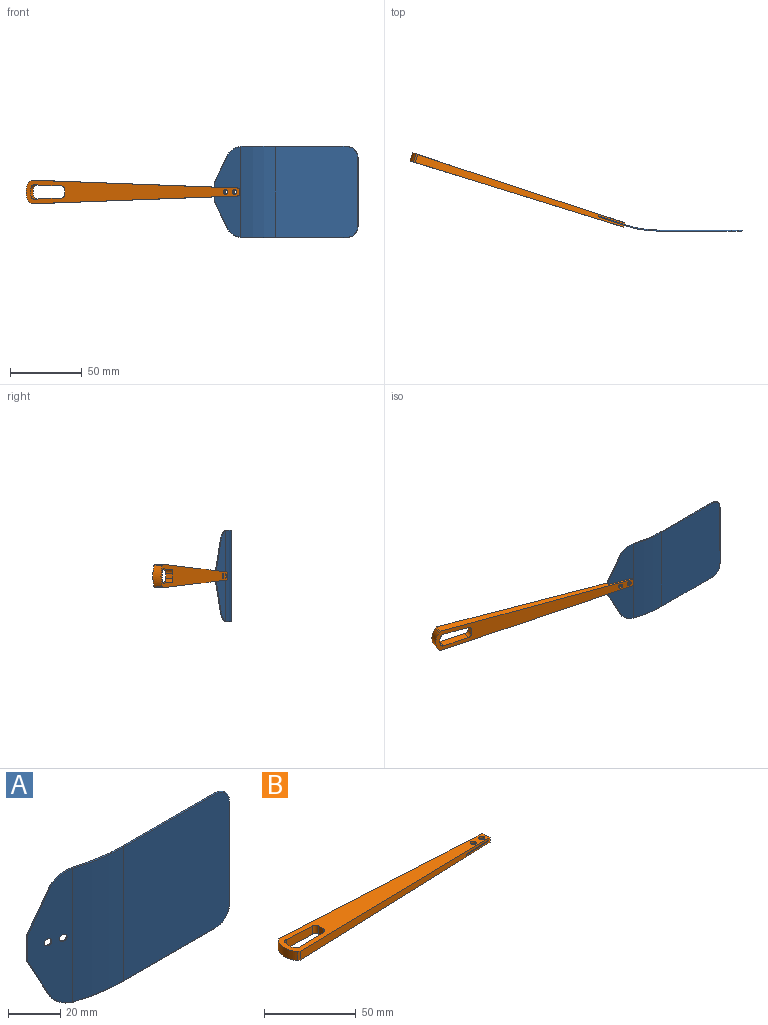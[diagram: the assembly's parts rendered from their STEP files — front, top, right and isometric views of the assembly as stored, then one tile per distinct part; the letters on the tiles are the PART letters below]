
ASSEMBLY  parts=2 mates=1
PART A: 24 faces, bbox 100.9x11.4x65.5 mm
  f0: plane 62.81x18.59mm, normal (-0.31,-0.95,0), area 862.8mm2, adj f1,f6,f7,f8,f9,f10,f21,f23
  f1: cylinder r=76.2mm len=62.89mm, axis (0,0,-1), area 1525.4mm2, adj f0,f2,f12,f13,f19,f22
  f2: plane 62.89x57.31mm, normal (0,-1,0), area 3581.6mm2, adj f1,f14,f15,f16,f17,f18
  f3: plane 62.89x57.31mm, normal (0,1,0), area 3581.6mm2, adj f4,f14,f15,f16,f17,f18
  f4: cylinder r=75.59mm len=62.89mm, axis (0,0,-1), area 1513.2mm2, adj f3,f5,f11,f12,f19,f20
  f5: plane 62.81x18.59mm, normal (0.31,0.95,0), area 862.8mm2, adj f4,f6,f7,f8,f9,f10,f21,f23
  f6: plane 12.7x0.58mm, normal (-0.95,0.31,0), area 7.6mm2, adj f0,f5,f9,f23
  f7: cylinder r=1.61mm len=3.25mm, axis (0.31,0.95,0), area 6.2mm2, adj f0,f5
  f8: cylinder r=1.61mm len=3.25mm, axis (0.31,0.95,0), area 6.2mm2, adj f0,f5
  f9: cylinder r=0.3mm len=19.06mm, axis (-0.42,0.14,0.89), area 19.9mm2, adj f0,f5,f6,f10
  f10: torus R=12.4mm, axis (0.31,0.95,0), area 12.4mm2, adj f0,f5,f9,f11,f13
  f11: bspline ~4.86x1.83mm, area 0.5mm2, adj f4,f10,f12,f13
  f12: torus R=75.9mm, axis (0,0,1), area 22.2mm2, adj f1,f4,f11,f13,f14
  f13: bspline ~4.87x1.83mm, area 0.5mm2, adj f1,f10,f11,f12
  f14: cylinder r=0.3mm len=50mm, axis (-1,0,0), area 47.9mm2, adj f2,f3,f12,f15
  f15: torus R=7.32mm, axis (0,1,0), area 11.3mm2, adj f2,f3,f14,f16
  f16: cylinder r=0.3mm len=48.26mm, axis (0,0,-1), area 46.2mm2, adj f2,f3,f15,f17
  f17: torus R=7.32mm, axis (0,1,0), area 11.3mm2, adj f2,f3,f16,f18
  f18: cylinder r=0.3mm len=50mm, axis (1,0,0), area 47.9mm2, adj f2,f3,f17,f19
  f19: torus R=75.9mm, axis (0,0,1), area 22.2mm2, adj f1,f4,f18,f20,f22
  f20: bspline ~4.86x1.83mm, area 0.5mm2, adj f4,f19,f21,f22
  f21: torus R=12.4mm, axis (0.31,0.95,0), area 12.4mm2, adj f0,f5,f20,f22,f23
  f22: bspline ~4.87x1.83mm, area 0.5mm2, adj f1,f19,f20,f21
  f23: cylinder r=0.3mm len=19.06mm, axis (-0.42,0.14,-0.89), area 19.9mm2, adj f0,f5,f6,f21
PART B: 24 faces, bbox 155.5x16.5x6 mm
  f0: plane 5.43x1.28mm, normal (1,0,0), area 7mm2, adj f1,f2,f13,f21
  f1: plane 151.61x5.88mm, normal (0.04,1,0), area 675.4mm2, adj f0,f11,f13,f14,f20,f21,f22,f23
  f2: plane 151.61x5.88mm, normal (0.04,-1,0), area 675.4mm2, adj f0,f11,f13,f14,f19,f21,f22,f23
  f3: cylinder r=1.61mm len=3.23mm, axis (0,0,-1), area 13mm2, adj f13,f21
  f4: cylinder r=1.61mm len=3.23mm, axis (0,0,-1), area 14.8mm2, adj f14,f22
  f5: cylinder r=1.61mm len=3.23mm, axis (0,0,-1), area 13mm2, adj f13,f21
  f6: cylinder r=1.61mm len=3.23mm, axis (0,0,-1), area 13.6mm2, adj f14,f22
  f7: cylinder r=12.73mm len=15.18mm, axis (0,0,-1), area 96.6mm2, adj f13,f14,f19,f20
  f8: cylinder r=9.57mm len=6.6mm, axis (0,0,-1), area 39.7mm2, adj f13,f14,f16,f17
  f9: plane 19.41x5.84mm, normal (-0.04,-1,0), area 110.1mm2, adj f13,f14,f15,f16
  f10: plane 5.45x3.43mm, normal (-1,0,0), area 18.7mm2, adj f13,f14,f15,f18
  f11: plane 5.43x1.28mm, normal (1,0,0), area 7mm2, adj f1,f2,f14,f22
  f12: plane 19.42x5.84mm, normal (-0.04,1,0), area 110.1mm2, adj f13,f14,f17,f18
  f13: plane 155.44x16.45mm, normal (0,0,-1), area 1467mm2, adj f0,f1,f2,f3,f5,f7,f8,f9
  f14: plane 155.46x16.47mm, normal (0.02,0,1), area 1467.2mm2, adj f1,f2,f4,f6,f7,f8,f9,f10
  f15: cylinder r=2.54mm len=5.49mm, axis (0,0,1), area 21.3mm2, adj f9,f10,f13,f14
  f16: cylinder r=2.54mm len=5.88mm, axis (0,0,-1), area 18.7mm2, adj f8,f9,f13,f14
  f17: cylinder r=2.54mm len=5.88mm, axis (0,0,-1), area 18.7mm2, adj f8,f12,f13,f14
  f18: cylinder r=2.54mm len=5.49mm, axis (0,0,1), area 21.3mm2, adj f10,f12,f13,f14
  f19: plane 5.91x1.32mm, normal (-0.43,-0.9,0), area 8.6mm2, adj f2,f7,f13,f14
  f20: plane 5.91x1.32mm, normal (-0.43,0.9,0), area 8.6mm2, adj f1,f7,f13,f14
  f21: plane 19.05x6.81mm, normal (0,0,1), area 100.2mm2, adj f0,f1,f2,f3,f5,f23
  f22: plane 19.05x6.81mm, normal (0,0,-1), area 100.2mm2, adj f1,f2,f4,f6,f11,f23
  f23: plane 6.81x0.61mm, normal (1,0,0), area 4.2mm2, adj f1,f2,f21,f22
PLACE A t=(0,28.96,0)mm
PLACE B rot(axis=(0.98,-0.16,-0.16),91.4deg) t=(19.28,10.75,52.21)mm
MATE fastened B.f3 <-> A.f7  axis (-0.31,-0.95,0) through (90.87,-14.19,31.75)mm
